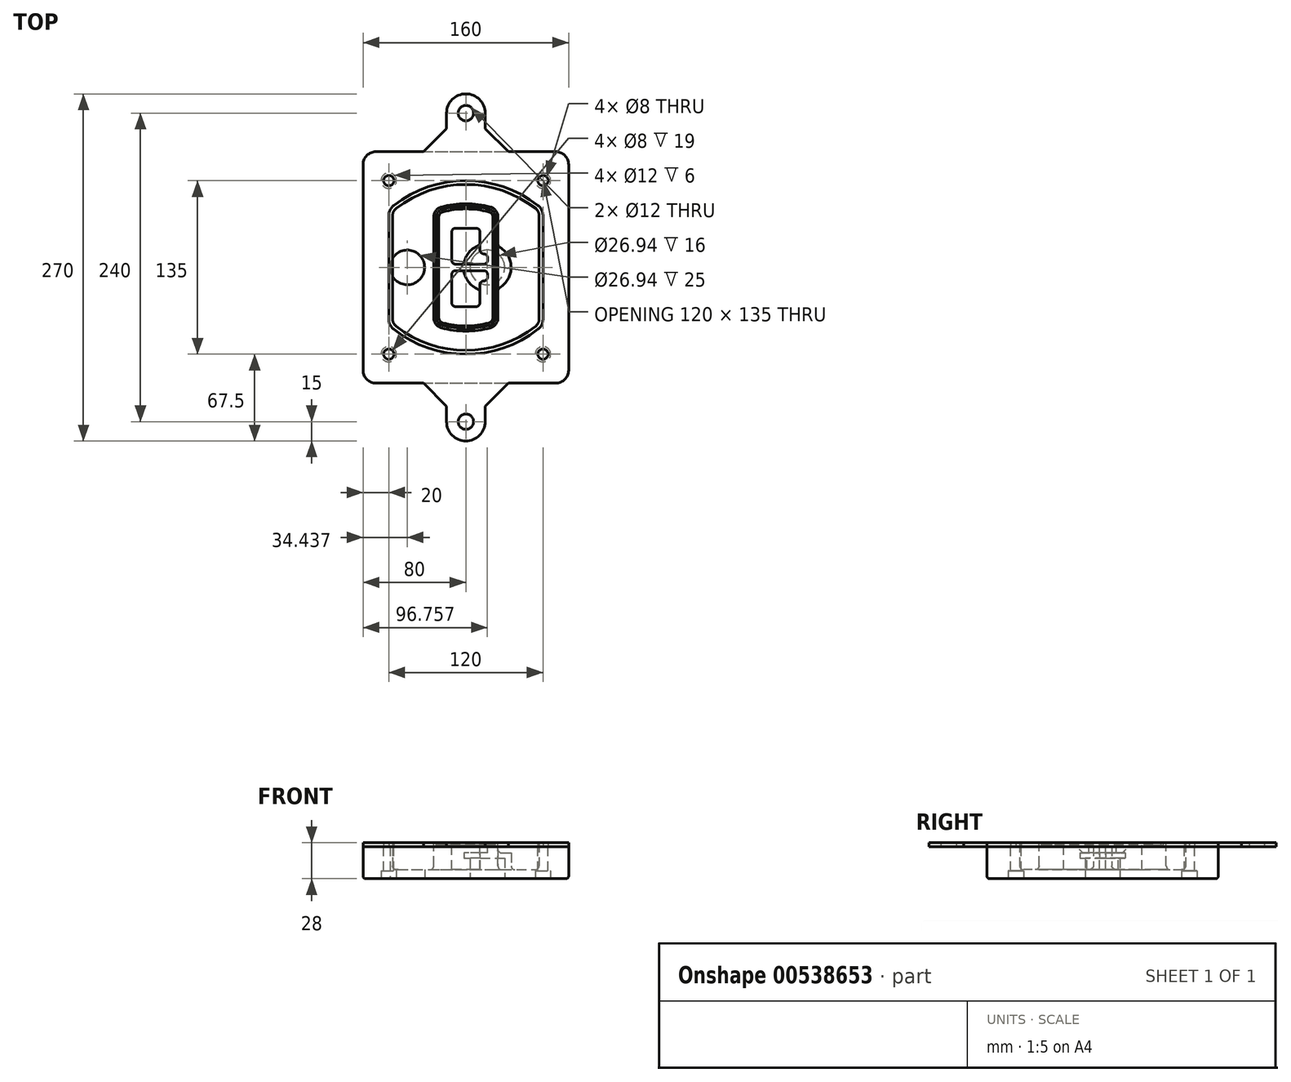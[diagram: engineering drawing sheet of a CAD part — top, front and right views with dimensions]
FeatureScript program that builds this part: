
annotation { "Feature Type Name" : "Feature", "Feature Type Description" : "" }
export const myFeature = defineFeature(function(context is Context, id is Id, definition is map)
    precondition{}
    {
        {
            var Q0;
            Q0=qCreatedBy(makeId("Top.planeOp"),FACE);
            var sketch = newSketch(context, id + "F0", { "sketchPlane" : qUnion([Q0])});
            skPoint(sketch, "E0.rect.middle", {"position": v(0, 0) * mm});
            skLineSegment(sketch, "E1.bottom", {"start": v(-70, -90) * mm, "end": v(70, -90) * mm});
            skLineSegment(sketch, "E1.top", {"start": v(-70, 90) * mm, "end": v(70, 90) * mm});
            skLineSegment(sketch, "E1.left", {"start": v(-80, -80) * mm, "end": v(-80, 80) * mm});
            skLineSegment(sketch, "E1.right", {"start": v(80, -80) * mm, "end": v(80, 80) * mm});
            skLineSegment(sketch, "E2", {"start": v(-80, 90) * mm, "end": v(80, -90) * mm, "construction": true});
            skLineSegment(sketch, "E3", {"start": v(80, 90) * mm, "end": v(-80, -90) * mm, "construction": true});
            skCircle(sketch, "E4", {"center": v(-60, 67.5) * mm, "radius": 4 * mm});
            skCircle(sketch, "E5", {"center": v(60, 67.5) * mm, "radius": 4 * mm});
            skCircle(sketch, "E6", {"center": v(60, -67.5) * mm, "radius": 4 * mm});
            skCircle(sketch, "E7", {"center": v(-60, -67.5) * mm, "radius": 4 * mm});
            skLineSegment(sketch, "E8", {"start": v(-60, 67.5) * mm, "end": v(60, 67.5) * mm, "construction": true});
            skLineSegment(sketch, "E9", {"start": v(60, 67.5) * mm, "end": v(60, -67.5) * mm, "construction": true});
            skLineSegment(sketch, "E10", {"start": v(60, -67.5) * mm, "end": v(-60, -67.5) * mm, "construction": true});
            skLineSegment(sketch, "E11", {"start": v(-60, -67.5) * mm, "end": v(-60, 67.5) * mm, "construction": true});
            skLineSegment(sketch, "E12", {"start": v(-60, 40.3) * mm, "end": v(-60, -40.3) * mm});
            skLineSegment(sketch, "E13", {"start": v(60, 40.3) * mm, "end": v(60, -40.3) * mm});
            skArc(sketch, "E14", {"start": v(56.15, 48.18) * mm, "mid": v(0, 67.5) * mm, "end": v(-56.15, 48.18) * mm});
            skArc(sketch, "E15", {"start": v(-56.15, -48.18) * mm, "mid": v(0, -67.5) * mm, "end": v(56.15, -48.18) * mm});
            skLineSegment(sketch, "E16", {"start": v(-60, 0) * mm, "end": v(60, 0) * mm, "construction": true});
            skPoint(sketch, "E17.visualSharp", {"position": v(-60, -45) * mm});
            skArc(sketch, "E17.filletArc", {"start": v(-60, -40.3) * mm, "mid": v(-58.99, -44.68) * mm, "end": v(-56.15, -48.18) * mm});
            skPoint(sketch, "E18.visualSharp", {"position": v(-60, 45) * mm});
            skArc(sketch, "E18.filletArc", {"start": v(-56.15, 48.18) * mm, "mid": v(-58.99, 44.68) * mm, "end": v(-60, 40.3) * mm});
            skPoint(sketch, "E19.visualSharp", {"position": v(60, 45) * mm});
            skArc(sketch, "E19.filletArc", {"start": v(60, 40.3) * mm, "mid": v(58.99, 44.68) * mm, "end": v(56.15, 48.18) * mm});
            skPoint(sketch, "E20.visualSharp", {"position": v(60, -45) * mm});
            skArc(sketch, "E20.filletArc", {"start": v(56.15, -48.18) * mm, "mid": v(58.99, -44.68) * mm, "end": v(60, -40.3) * mm});
            skPoint(sketch, "E21.visualSharp", {"position": v(-80, 90) * mm});
            skArc(sketch, "E21.filletArc", {"start": v(-70, 90) * mm, "mid": v(-77.07, 87.07) * mm, "end": v(-80, 80) * mm});
            skPoint(sketch, "E22.visualSharp", {"position": v(80, 90) * mm});
            skArc(sketch, "E22.filletArc", {"start": v(80, 80) * mm, "mid": v(77.07, 87.07) * mm, "end": v(70, 90) * mm});
            skPoint(sketch, "E23.visualSharp", {"position": v(80, -90) * mm});
            skArc(sketch, "E23.filletArc", {"start": v(70, -90) * mm, "mid": v(77.07, -87.07) * mm, "end": v(80, -80) * mm});
            skPoint(sketch, "E24.visualSharp", {"position": v(-80, -90) * mm});
            skArc(sketch, "E24.filletArc", {"start": v(-80, -80) * mm, "mid": v(-77.07, -87.07) * mm, "end": v(-70, -90) * mm});
            skArc(sketch, "E25.0", {"start": v(57, 40.3) * mm, "mid": v(56.3, 43.36) * mm, "end": v(54.3, 45.81) * mm});
            skLineSegment(sketch, "E25.1", {"start": v(57, 40.3) * mm, "end": v(57, -40.3) * mm});
            skArc(sketch, "E25.2", {"start": v(54.3, -45.81) * mm, "mid": v(56.3, -43.36) * mm, "end": v(57, -40.3) * mm});
            skArc(sketch, "E25.3", {"start": v(-54.3, -45.81) * mm, "mid": v(0, -64.5) * mm, "end": v(54.3, -45.81) * mm});
            skArc(sketch, "E25.4", {"start": v(-57, -40.3) * mm, "mid": v(-56.3, -43.36) * mm, "end": v(-54.3, -45.81) * mm});
            skArc(sketch, "E25.5", {"start": v(54.3, 45.81) * mm, "mid": v(0, 64.5) * mm, "end": v(-54.3, 45.81) * mm});
            skLineSegment(sketch, "E25.6", {"start": v(-57, 40.3) * mm, "end": v(-57, -40.3) * mm});
            skArc(sketch, "E25.7", {"start": v(-54.3, 45.81) * mm, "mid": v(-56.3, 43.36) * mm, "end": v(-57, 40.3) * mm});
            skArc(sketch, "E26.0", {"start": v(-58.62, 51.33) * mm, "mid": v(-62.58, 46.43) * mm, "end": v(-64, 40.3) * mm});
            skArc(sketch, "E26.1", {"start": v(58.62, 51.33) * mm, "mid": v(0, 71.5) * mm, "end": v(-58.62, 51.33) * mm});
            skArc(sketch, "E26.2", {"start": v(64, 40.3) * mm, "mid": v(62.58, 46.43) * mm, "end": v(58.62, 51.33) * mm});
            skLineSegment(sketch, "E26.3", {"start": v(64, 40.3) * mm, "end": v(64, -40.3) * mm});
            skArc(sketch, "E26.4", {"start": v(58.62, -51.33) * mm, "mid": v(62.58, -46.43) * mm, "end": v(64, -40.3) * mm});
            skLineSegment(sketch, "E26.5", {"start": v(-64, 40.3) * mm, "end": v(-64, -40.3) * mm});
            skArc(sketch, "E26.6", {"start": v(-58.62, -51.33) * mm, "mid": v(0, -71.5) * mm, "end": v(58.62, -51.33) * mm});
            skArc(sketch, "E26.7", {"start": v(-64, -40.3) * mm, "mid": v(-62.58, -46.43) * mm, "end": v(-58.62, -51.33) * mm});
            skSolve(sketch);
        }
        {
            var Q0;
            Q0=makeQuery(id+"F0.imprint","IMPRINT",FACE,{"disambiguationData":[TD([[makeQuery(id+"F0.imprint","IMPRINT",EDGE,{"derivedFrom":sQuery(id+"F0.wireOp",EDGE,"E1.bottom")}),1.0]])]});
            var Q1;
            Q1=makeQuery(id+"F0.imprint","IMPRINT",FACE,{"disambiguationData":[TD([[makeQuery(id+"F0.imprint","IMPRINT",EDGE,{"derivedFrom":sQuery(id+"F0.wireOp",EDGE,"E12")}),1.0]])]});
            var Q2;
            Q2=makeQuery(id+"F0.imprint","IMPRINT",FACE,{"disambiguationData":[TD([[makeQuery(id+"F0.imprint","IMPRINT",EDGE,{"derivedFrom":sQuery(id+"F0.wireOp",EDGE,"E25.0")}),1.0]])]});
            var Q3;
            Q3=makeQuery(id+"F0.imprint","IMPRINT",FACE,{"disambiguationData":[TD([[makeQuery(id+"F0.imprint","IMPRINT",EDGE,{"derivedFrom":sQuery(id+"F0.wireOp",EDGE,"E12")}),-1.0]])]});
            extrude(context, id + "F1", {"entities" : qUnion([Q0, Q1, Q2, Q3]), "oppositeDirection" : true, "depth" : 25 * mm});
        }
        {
            var Q0;
            Q0=makeQuery(id+"F0.imprint","IMPRINT",FACE,{"disambiguationData":[TD([[makeQuery(id+"F0.imprint","IMPRINT",EDGE,{"derivedFrom":sQuery(id+"F0.wireOp",EDGE,"E12")}),1.0]])]});
            extrude(context, id + "F2", {"entities" : qUnion([Q0]), "operationType" : NewBodyOperationType.ADD, "depth" : 3 * mm});
        }
        {
            var Q0;
            Q0=makeQuery(id+"F0.imprint","IMPRINT",FACE,{"disambiguationData":[TD([[makeQuery(id+"F0.imprint","IMPRINT",EDGE,{"derivedFrom":sQuery(id+"F0.wireOp",EDGE,"E25.0")}),1.0]])]});
            extrude(context, id + "F3", {"entities" : qUnion([Q0]), "operationType" : NewBodyOperationType.REMOVE, "oppositeDirection" : true, "depth" : 18 * mm});
        }
        {
            var Q0;
            Q0=makeQuery(id+"F2.opExtrude","CAP_FACE",FACE,{"disambiguationData":[OSD([sQuery(id+"F0.wireOp",EDGE,"E12"),sQuery(id+"F0.wireOp",EDGE,"E13"),sQuery(id+"F0.wireOp",EDGE,"E14"),sQuery(id+"F0.wireOp",EDGE,"E15"),sQuery(id+"F0.wireOp",EDGE,"E17.filletArc"),sQuery(id+"F0.wireOp",EDGE,"E18.filletArc"),sQuery(id+"F0.wireOp",EDGE,"E19.filletArc"),sQuery(id+"F0.wireOp",EDGE,"E20.filletArc"),sQuery(id+"F0.wireOp",EDGE,"E25.0"),sQuery(id+"F0.wireOp",EDGE,"E25.1"),sQuery(id+"F0.wireOp",EDGE,"E25.2"),sQuery(id+"F0.wireOp",EDGE,"E25.3"),sQuery(id+"F0.wireOp",EDGE,"E25.4"),sQuery(id+"F0.wireOp",EDGE,"E25.5"),sQuery(id+"F0.wireOp",EDGE,"E25.6"),sQuery(id+"F0.wireOp",EDGE,"E25.7")])],"isStart":false});
            var sketch = newSketch(context, id + "F4", { "sketchPlane" : qUnion([Q0])});
            skArc(sketch, "E27.0", {"start": v(-19.08, -46.97) * mm, "mid": v(0, -49.5) * mm, "end": v(19.08, -46.97) * mm});
            skArc(sketch, "E28.0", {"start": v(19.08, 46.97) * mm, "mid": v(0, 49.5) * mm, "end": v(-19.08, 46.97) * mm});
            skLineSegment(sketch, "E29", {"start": v(-25, 39.25) * mm, "end": v(-25, -39.25) * mm});
            skLineSegment(sketch, "E30", {"start": v(25, 39.25) * mm, "end": v(25, -39.25) * mm});
            skLineSegment(sketch, "E31", {"start": v(-25, 45.1) * mm, "end": v(25, 45.1) * mm, "construction": true});
            skLineSegment(sketch, "E32", {"start": v(-25, -45.1) * mm, "end": v(25, -45.1) * mm, "construction": true});
            skPoint(sketch, "E33.visualSharp", {"position": v(-25, 45.1) * mm});
            skArc(sketch, "E33.filletArc", {"start": v(-19.08, 46.97) * mm, "mid": v(-23.35, 44.11) * mm, "end": v(-25, 39.25) * mm});
            skPoint(sketch, "E34.visualSharp", {"position": v(25, 45.1) * mm});
            skArc(sketch, "E34.filletArc", {"start": v(25, 39.25) * mm, "mid": v(23.35, 44.11) * mm, "end": v(19.08, 46.97) * mm});
            skPoint(sketch, "E35.visualSharp", {"position": v(25, -45.1) * mm});
            skArc(sketch, "E35.filletArc", {"start": v(19.08, -46.97) * mm, "mid": v(23.35, -44.11) * mm, "end": v(25, -39.25) * mm});
            skPoint(sketch, "E36.visualSharp", {"position": v(-25, -45.1) * mm});
            skArc(sketch, "E36.filletArc", {"start": v(-25, -39.25) * mm, "mid": v(-23.35, -44.11) * mm, "end": v(-19.08, -46.97) * mm});
            skArc(sketch, "E37.0", {"start": v(54.3, 45.81) * mm, "mid": v(0, 64.5) * mm, "end": v(-54.3, 45.81) * mm});
            skArc(sketch, "E37.1", {"start": v(-54.3, 45.81) * mm, "mid": v(-56.3, 43.36) * mm, "end": v(-57, 40.3) * mm});
            skLineSegment(sketch, "E37.2", {"start": v(-57, 40.3) * mm, "end": v(-57, -40.3) * mm});
            skArc(sketch, "E37.3", {"start": v(-57, -40.3) * mm, "mid": v(-56.3, -43.36) * mm, "end": v(-54.3, -45.81) * mm});
            skArc(sketch, "E37.4", {"start": v(-54.3, -45.81) * mm, "mid": v(0, -64.5) * mm, "end": v(54.3, -45.81) * mm});
            skArc(sketch, "E37.5", {"start": v(54.3, -45.81) * mm, "mid": v(56.3, -43.36) * mm, "end": v(57, -40.3) * mm});
            skLineSegment(sketch, "E37.6", {"start": v(57, 40.3) * mm, "end": v(57, -40.3) * mm});
            skArc(sketch, "E37.7", {"start": v(57, 40.3) * mm, "mid": v(56.3, 43.36) * mm, "end": v(54.3, 45.81) * mm});
            skLineSegment(sketch, "E38.0", {"start": v(23, 39.25) * mm, "end": v(23, -39.25) * mm});
            skArc(sketch, "E38.1", {"start": v(18.56, -45.04) * mm, "mid": v(21.76, -42.9) * mm, "end": v(23, -39.25) * mm});
            skArc(sketch, "E38.2", {"start": v(-18.56, -45.04) * mm, "mid": v(0, -47.5) * mm, "end": v(18.56, -45.04) * mm});
            skArc(sketch, "E38.3", {"start": v(-23, -39.25) * mm, "mid": v(-21.76, -42.9) * mm, "end": v(-18.56, -45.04) * mm});
            skLineSegment(sketch, "E38.4", {"start": v(-23, 39.25) * mm, "end": v(-23, -39.25) * mm});
            skArc(sketch, "E38.5", {"start": v(23, 39.25) * mm, "mid": v(21.76, 42.9) * mm, "end": v(18.56, 45.04) * mm});
            skArc(sketch, "E38.6", {"start": v(-18.56, 45.04) * mm, "mid": v(-21.76, 42.9) * mm, "end": v(-23, 39.25) * mm});
            skArc(sketch, "E38.7", {"start": v(18.56, 45.04) * mm, "mid": v(0, 47.5) * mm, "end": v(-18.56, 45.04) * mm});
            skArc(sketch, "E39.0", {"start": v(21, 39.25) * mm, "mid": v(20.18, 41.68) * mm, "end": v(18.04, 43.1) * mm});
            skLineSegment(sketch, "E39.1", {"start": v(21, 39.25) * mm, "end": v(21, -39.25) * mm});
            skArc(sketch, "E39.2", {"start": v(18.04, -43.1) * mm, "mid": v(20.18, -41.68) * mm, "end": v(21, -39.25) * mm});
            skArc(sketch, "E39.3", {"start": v(-18.04, -43.1) * mm, "mid": v(0, -45.5) * mm, "end": v(18.04, -43.1) * mm});
            skArc(sketch, "E39.4", {"start": v(-21, -39.25) * mm, "mid": v(-20.18, -41.68) * mm, "end": v(-18.04, -43.1) * mm});
            skArc(sketch, "E39.5", {"start": v(18.04, 43.1) * mm, "mid": v(0, 45.5) * mm, "end": v(-18.04, 43.1) * mm});
            skLineSegment(sketch, "E39.6", {"start": v(-21, 39.25) * mm, "end": v(-21, -39.25) * mm});
            skArc(sketch, "E39.7", {"start": v(-18.04, 43.1) * mm, "mid": v(-20.18, 41.68) * mm, "end": v(-21, 39.25) * mm});
            skLineSegment(sketch, "E40", {"start": v(-25, 0) * mm, "end": v(25, 0) * mm, "construction": true});
            skLineSegment(sketch, "E41", {"start": v(-11, 5.5) * mm, "end": v(-11, 27.5) * mm});
            skLineSegment(sketch, "E42", {"start": v(-8, 30.5) * mm, "end": v(8, 30.5) * mm});
            skLineSegment(sketch, "E43", {"start": v(11, 27.5) * mm, "end": v(11, 13.5) * mm});
            skLineSegment(sketch, "E44", {"start": v(14, 10.5) * mm, "end": v(14, 10.5) * mm});
            skLineSegment(sketch, "E45", {"start": v(17, 7.5) * mm, "end": v(17, 5.5) * mm});
            skLineSegment(sketch, "E46", {"start": v(14, 2.5) * mm, "end": v(-8, 2.5) * mm});
            skPoint(sketch, "E47.visualSharp", {"position": v(-11, 30.5) * mm});
            skArc(sketch, "E47.filletArc", {"start": v(-8, 30.5) * mm, "mid": v(-10.12, 29.62) * mm, "end": v(-11, 27.5) * mm});
            skPoint(sketch, "E48.visualSharp", {"position": v(11, 30.5) * mm});
            skArc(sketch, "E48.filletArc", {"start": v(11, 27.5) * mm, "mid": v(10.12, 29.62) * mm, "end": v(8, 30.5) * mm});
            skPoint(sketch, "E49.visualSharp", {"position": v(11, 10.5) * mm});
            skArc(sketch, "E49.filletArc", {"start": v(11, 13.5) * mm, "mid": v(11.88, 11.38) * mm, "end": v(14, 10.5) * mm});
            skPoint(sketch, "E50.visualSharp", {"position": v(17, 10.5) * mm});
            skArc(sketch, "E50.filletArc", {"start": v(17, 7.5) * mm, "mid": v(16.12, 9.62) * mm, "end": v(14, 10.5) * mm});
            skPoint(sketch, "E51.visualSharp", {"position": v(17, 2.5) * mm});
            skArc(sketch, "E51.filletArc", {"start": v(14, 2.5) * mm, "mid": v(16.12, 3.38) * mm, "end": v(17, 5.5) * mm});
            skPoint(sketch, "E52.visualSharp", {"position": v(-11, 2.5) * mm});
            skArc(sketch, "E52.filletArc", {"start": v(-11, 5.5) * mm, "mid": v(-10.12, 3.38) * mm, "end": v(-8, 2.5) * mm});
            skLineSegment(sketch, "E53.0.MirrorCS", {"start": v(14, -2.5) * mm, "end": v(-8, -2.5) * mm});
            skArc(sketch, "E54.0.MirrorCS", {"start": v(-11, -5.5) * mm, "mid": v(-10.12, -3.38) * mm, "end": v(-8, -2.5) * mm});
            skLineSegment(sketch, "E55.0.MirrorCS", {"start": v(-11, -5.5) * mm, "end": v(-11, -27.5) * mm});
            skArc(sketch, "E56.0.MirrorCS", {"start": v(-8, -30.5) * mm, "mid": v(-10.12, -29.62) * mm, "end": v(-11, -27.5) * mm});
            skLineSegment(sketch, "E57.0.MirrorCS", {"start": v(-8, -30.5) * mm, "end": v(8, -30.5) * mm});
            skArc(sketch, "E58.0.MirrorCS", {"start": v(11, -27.5) * mm, "mid": v(10.12, -29.62) * mm, "end": v(8, -30.5) * mm});
            skLineSegment(sketch, "E59.0.MirrorCS", {"start": v(11, -27.5) * mm, "end": v(11, -13.5) * mm});
            skArc(sketch, "E60.0.MirrorCS", {"start": v(11, -13.5) * mm, "mid": v(11.88, -11.38) * mm, "end": v(14, -10.5) * mm});
            skArc(sketch, "E61.0.MirrorCS", {"start": v(17, -7.5) * mm, "mid": v(16.12, -9.62) * mm, "end": v(14, -10.5) * mm});
            skLineSegment(sketch, "E62.0.MirrorCS", {"start": v(17, -7.5) * mm, "end": v(17, -5.5) * mm});
            skArc(sketch, "E63.0.MirrorCS", {"start": v(14, -2.5) * mm, "mid": v(16.12, -3.38) * mm, "end": v(17, -5.5) * mm});
            skSolve(sketch);
        }
        {
            var Q0;
            Q0=makeQuery(id+"F4.imprint","IMPRINT",FACE,{"disambiguationData":[TD([[makeQuery(id+"F4.imprint","IMPRINT",EDGE,{"derivedFrom":sQuery(id+"F4.wireOp",EDGE,"E27.0")}),1.0]])]});
            var Q1;
            Q1=makeQuery(id+"F4.imprint","IMPRINT",FACE,{"disambiguationData":[TD([[makeQuery(id+"F4.imprint","IMPRINT",EDGE,{"derivedFrom":sQuery(id+"F4.wireOp",EDGE,"E38.0")}),-1.0]])]});
            var Q2;
            Q2=makeQuery(id+"F4.imprint","IMPRINT",FACE,{"disambiguationData":[TD([[makeQuery(id+"F4.imprint","IMPRINT",EDGE,{"derivedFrom":sQuery(id+"F4.wireOp",EDGE,"E39.0")}),1.0]])]});
            extrude(context, id + "F5", {"entities" : qUnion([Q0, Q1, Q2]), "operationType" : NewBodyOperationType.ADD, "endBound" : BoundingType.UP_TO_NEXT, "oppositeDirection" : true, "depth" : 25 * mm});
        }
        {
            var Q0;
            Q0=makeQuery(id+"F4.imprint","IMPRINT",FACE,{"disambiguationData":[TD([[makeQuery(id+"F4.imprint","IMPRINT",EDGE,{"derivedFrom":sQuery(id+"F4.wireOp",EDGE,"E38.0")}),-1.0]])]});
            extrude(context, id + "F6", {"entities" : qUnion([Q0]), "operationType" : NewBodyOperationType.REMOVE, "oppositeDirection" : true, "depth" : 2 * mm});
        }
        {
            var Q0;
            Q0=makeQuery(id+"F1.opExtrude","CAP_FACE",FACE,{"disambiguationData":[OSD([sQuery(id+"F0.wireOp",EDGE,"E1.bottom"),sQuery(id+"F0.wireOp",EDGE,"E1.top"),sQuery(id+"F0.wireOp",EDGE,"E1.left"),sQuery(id+"F0.wireOp",EDGE,"E1.right"),sQuery(id+"F0.wireOp",EDGE,"E4"),sQuery(id+"F0.wireOp",EDGE,"E5"),sQuery(id+"F0.wireOp",EDGE,"E6"),sQuery(id+"F0.wireOp",EDGE,"E7"),sQuery(id+"F0.wireOp",EDGE,"E21.filletArc"),sQuery(id+"F0.wireOp",EDGE,"E22.filletArc"),sQuery(id+"F0.wireOp",EDGE,"E23.filletArc"),sQuery(id+"F0.wireOp",EDGE,"E24.filletArc")])],"isStart":false});
            var sketch = newSketch(context, id + "F7", { "sketchPlane" : qUnion([Q0])});
            skCircle(sketch, "E64", {"center": v(16.76, 0) * mm, "radius": 13.47 * mm});
            skCircle(sketch, "E65", {"center": v(-45.56, 0) * mm, "radius": 13.47 * mm});
            skLineSegment(sketch, "E66", {"start": v(80, 0) * mm, "end": v(-80, 0) * mm});
            skCircle(sketch, "E67", {"center": v(16.76, 0) * mm, "radius": 18.47 * mm});
            skCircle(sketch, "E68", {"center": v(60, -67.5) * mm, "radius": 6 * mm});
            skCircle(sketch, "E69", {"center": v(-60, -67.5) * mm, "radius": 6 * mm});
            skCircle(sketch, "E70", {"center": v(-60, 67.5) * mm, "radius": 6 * mm});
            skCircle(sketch, "E71", {"center": v(60, 67.5) * mm, "radius": 6 * mm});
            skSolve(sketch);
        }
        {
            var Q0;
            {var subQ1=sQuery(id+"F7.wireOp",EDGE,"E66");var subQ4=sQuery(id+"F7.wireOp",EDGE,"E64");var subQ6=makeQuery(id+"F7.imprint","INTERSECT",VERTEX,{"disambiguationData":[OD(0.0)],"derivedFrom":[subQ4,subQ1]});Q0=makeQuery(id+"F7.imprint","IMPRINT",FACE,{"disambiguationData":[TD([[makeQuery(id+"F7.imprint","IMPRINT",EDGE,{"disambiguationData":[TD([[subQ6,-1.0]])],"derivedFrom":subQ4}),-1.0]])]});}
            var Q1;
            {var subQ0=sQuery(id+"F7.wireOp",EDGE,"E66");var subQ1=sQuery(id+"F7.wireOp",EDGE,"E64");var subQ3=makeQuery(id+"F7.imprint","INTERSECT",VERTEX,{"disambiguationData":[OD(0.0)],"derivedFrom":[subQ1,subQ0]});Q1=makeQuery(id+"F7.imprint","IMPRINT",FACE,{"disambiguationData":[TD([[makeQuery(id+"F7.imprint","IMPRINT",EDGE,{"disambiguationData":[TD([[subQ3,-1.0]])],"derivedFrom":subQ1}),1.0]])]});}
            var Q2;
            {var subQ0=sQuery(id+"F7.wireOp",EDGE,"E66");var subQ1=sQuery(id+"F7.wireOp",EDGE,"E64");var subQ3=makeQuery(id+"F7.imprint","INTERSECT",VERTEX,{"disambiguationData":[OD(0.0)],"derivedFrom":[subQ1,subQ0]});Q2=makeQuery(id+"F7.imprint","IMPRINT",FACE,{"disambiguationData":[TD([[makeQuery(id+"F7.imprint","IMPRINT",EDGE,{"disambiguationData":[TD([[subQ3,1.0]])],"derivedFrom":subQ1}),1.0]])]});}
            var Q3;
            {var subQ1=sQuery(id+"F7.wireOp",EDGE,"E66");var subQ4=sQuery(id+"F7.wireOp",EDGE,"E64");var subQ6=makeQuery(id+"F7.imprint","INTERSECT",VERTEX,{"disambiguationData":[OD(0.0)],"derivedFrom":[subQ4,subQ1]});Q3=makeQuery(id+"F7.imprint","IMPRINT",FACE,{"disambiguationData":[TD([[makeQuery(id+"F7.imprint","IMPRINT",EDGE,{"disambiguationData":[TD([[subQ6,1.0]])],"derivedFrom":subQ4}),-1.0]])]});}
            extrude(context, id + "F8", {"entities" : qUnion([Q0, Q1, Q2, Q3]), "operationType" : NewBodyOperationType.ADD, "oppositeDirection" : true, "depth" : 20 * mm});
        }
        {
            var Q0;
            {var subQ0=sQuery(id+"F7.wireOp",EDGE,"E66");var subQ1=sQuery(id+"F7.wireOp",EDGE,"E64");var subQ3=makeQuery(id+"F7.imprint","INTERSECT",VERTEX,{"disambiguationData":[OD(0.0)],"derivedFrom":[subQ1,subQ0]});Q0=makeQuery(id+"F7.imprint","IMPRINT",FACE,{"disambiguationData":[TD([[makeQuery(id+"F7.imprint","IMPRINT",EDGE,{"disambiguationData":[TD([[subQ3,-1.0]])],"derivedFrom":subQ1}),1.0]])]});}
            var Q1;
            {var subQ0=sQuery(id+"F7.wireOp",EDGE,"E66");var subQ1=sQuery(id+"F7.wireOp",EDGE,"E64");var subQ3=makeQuery(id+"F7.imprint","INTERSECT",VERTEX,{"disambiguationData":[OD(0.0)],"derivedFrom":[subQ1,subQ0]});Q1=makeQuery(id+"F7.imprint","IMPRINT",FACE,{"disambiguationData":[TD([[makeQuery(id+"F7.imprint","IMPRINT",EDGE,{"disambiguationData":[TD([[subQ3,1.0]])],"derivedFrom":subQ1}),1.0]])]});}
            extrude(context, id + "F9", {"entities" : qUnion([Q0, Q1]), "operationType" : NewBodyOperationType.REMOVE, "oppositeDirection" : true, "depth" : 16 * mm});
        }
        {
            var Q0;
            {var subQ0=sQuery(id+"F7.wireOp",EDGE,"E66");var subQ1=sQuery(id+"F7.wireOp",EDGE,"E65");var subQ3=makeQuery(id+"F7.imprint","INTERSECT",VERTEX,{"disambiguationData":[OD(0.0)],"derivedFrom":[subQ1,subQ0]});Q0=makeQuery(id+"F7.imprint","IMPRINT",FACE,{"disambiguationData":[TD([[makeQuery(id+"F7.imprint","IMPRINT",EDGE,{"disambiguationData":[TD([[subQ3,-1.0]])],"derivedFrom":subQ1}),1.0]])]});}
            var Q1;
            {var subQ0=sQuery(id+"F7.wireOp",EDGE,"E66");var subQ1=sQuery(id+"F7.wireOp",EDGE,"E65");var subQ3=makeQuery(id+"F7.imprint","INTERSECT",VERTEX,{"disambiguationData":[OD(0.0)],"derivedFrom":[subQ1,subQ0]});Q1=makeQuery(id+"F7.imprint","IMPRINT",FACE,{"disambiguationData":[TD([[makeQuery(id+"F7.imprint","IMPRINT",EDGE,{"disambiguationData":[TD([[subQ3,1.0]])],"derivedFrom":subQ1}),1.0]])]});}
            extrude(context, id + "F10", {"entities" : qUnion([Q0, Q1]), "operationType" : NewBodyOperationType.REMOVE, "oppositeDirection" : true, "depth" : 25 * mm});
        }
        {
            var Q0;
            Q0=makeQuery(id+"F7.imprint","IMPRINT",FACE,{"disambiguationData":[TD([[makeQuery(id+"F7.imprint","IMPRINT",EDGE,{"derivedFrom":sQuery(id+"F7.wireOp",EDGE,"E68")}),1.0]])]});
            var Q1;
            Q1=makeQuery(id+"F7.imprint","IMPRINT",FACE,{"disambiguationData":[TD([[makeQuery(id+"F7.imprint","IMPRINT",EDGE,{"derivedFrom":makeQuery(id+"F1.opExtrude","CAP_EDGE",EDGE,{"disambiguationData":[OSD([sQuery(id+"F0.wireOp",EDGE,"E5")])],"isStart":false})}),-1.0]])]});
            var Q2;
            Q2=makeQuery(id+"F7.imprint","IMPRINT",FACE,{"disambiguationData":[TD([[makeQuery(id+"F7.imprint","IMPRINT",EDGE,{"derivedFrom":sQuery(id+"F7.wireOp",EDGE,"E69")}),1.0]])]});
            var Q3;
            Q3=makeQuery(id+"F7.imprint","IMPRINT",FACE,{"disambiguationData":[TD([[makeQuery(id+"F7.imprint","IMPRINT",EDGE,{"derivedFrom":makeQuery(id+"F1.opExtrude","CAP_EDGE",EDGE,{"disambiguationData":[OSD([sQuery(id+"F0.wireOp",EDGE,"E4")])],"isStart":false})}),-1.0]])]});
            var Q4;
            Q4=makeQuery(id+"F7.imprint","IMPRINT",FACE,{"disambiguationData":[TD([[makeQuery(id+"F7.imprint","IMPRINT",EDGE,{"derivedFrom":sQuery(id+"F7.wireOp",EDGE,"E70")}),1.0]])]});
            var Q5;
            Q5=makeQuery(id+"F7.imprint","IMPRINT",FACE,{"disambiguationData":[TD([[makeQuery(id+"F7.imprint","IMPRINT",EDGE,{"derivedFrom":makeQuery(id+"F1.opExtrude","CAP_EDGE",EDGE,{"disambiguationData":[OSD([sQuery(id+"F0.wireOp",EDGE,"E7")])],"isStart":false})}),-1.0]])]});
            var Q6;
            Q6=makeQuery(id+"F7.imprint","IMPRINT",FACE,{"disambiguationData":[TD([[makeQuery(id+"F7.imprint","IMPRINT",EDGE,{"derivedFrom":sQuery(id+"F7.wireOp",EDGE,"E71")}),1.0]])]});
            var Q7;
            Q7=makeQuery(id+"F7.imprint","IMPRINT",FACE,{"disambiguationData":[TD([[makeQuery(id+"F7.imprint","IMPRINT",EDGE,{"derivedFrom":makeQuery(id+"F1.opExtrude","CAP_EDGE",EDGE,{"disambiguationData":[OSD([sQuery(id+"F0.wireOp",EDGE,"E6")])],"isStart":false})}),-1.0]])]});
            extrude(context, id + "F11", {"entities" : qUnion([Q0, Q1, Q2, Q3, Q4, Q5, Q6, Q7]), "operationType" : NewBodyOperationType.REMOVE, "oppositeDirection" : true, "depth" : 6 * mm});
        }
        {
            var Q0;
            Q0=makeQuery(id+"F9.boolean.opBoolean","COPY",FACE,{"derivedFrom":makeQuery(id+"F9.opExtrude","CAP_FACE",FACE,{"disambiguationData":[OSD([sQuery(id+"F7.wireOp",EDGE,"E64")])],"isStart":false})});
            var sketch = newSketch(context, id + "F12", { "sketchPlane" : qUnion([Q0])});
            skArc(sketch, "E72.0", {"start": v(11, 17.55) * mm, "mid": v(2.57, 11.82) * mm, "end": v(-1.54, 2.5) * mm});
            skArc(sketch, "E72.1", {"start": v(-1.54, -2.5) * mm, "mid": v(2.57, -11.82) * mm, "end": v(11, -17.55) * mm});
            skLineSegment(sketch, "E73", {"start": v(-1.54, -2.5) * mm, "end": v(14, -2.5) * mm});
            skLineSegment(sketch, "E74.0", {"start": v(14, 2.5) * mm, "end": v(-1.54, 2.5) * mm});
            skArc(sketch, "E74.1", {"start": v(14, 2.5) * mm, "mid": v(16.12, 3.38) * mm, "end": v(17, 5.5) * mm});
            skLineSegment(sketch, "E74.2", {"start": v(17, 7.5) * mm, "end": v(17, 5.5) * mm});
            skArc(sketch, "E74.3", {"start": v(17, 7.5) * mm, "mid": v(16.12, 9.62) * mm, "end": v(14, 10.5) * mm});
            skArc(sketch, "E74.4", {"start": v(11, 13.5) * mm, "mid": v(11.88, 11.38) * mm, "end": v(14, 10.5) * mm});
            skLineSegment(sketch, "E74.5", {"start": v(11, 17.55) * mm, "end": v(11, 13.5) * mm});
            skLineSegment(sketch, "E74.7", {"start": v(14, -2.5) * mm, "end": v(-1.54, -2.5) * mm});
            skArc(sketch, "E74.8", {"start": v(14, -2.5) * mm, "mid": v(16.12, -3.38) * mm, "end": v(17, -5.5) * mm});
            skLineSegment(sketch, "E74.9", {"start": v(17, -7.5) * mm, "end": v(17, -5.5) * mm});
            skArc(sketch, "E74.10", {"start": v(17, -7.5) * mm, "mid": v(16.12, -9.62) * mm, "end": v(14, -10.5) * mm});
            skArc(sketch, "E74.11", {"start": v(11, -13.5) * mm, "mid": v(11.88, -11.38) * mm, "end": v(14, -10.5) * mm});
            skLineSegment(sketch, "E74.12", {"start": v(11, -17.55) * mm, "end": v(11, -13.5) * mm});
            skPoint(sketch, "E75.orphan", {"position": v(11, -27.5) * mm});
            skPoint(sketch, "E76.orphan", {"position": v(-8, -2.5) * mm});
            skPoint(sketch, "E77.orphan", {"position": v(-8, 2.5) * mm});
            skPoint(sketch, "E78.orphan", {"position": v(11, 27.5) * mm});
            skSolve(sketch);
        }
        {
            var Q0;
            {var subQ7=sQuery(id+"F12.wireOp",EDGE,"E72.0");var subQ14=sQuery(id+"F12.wireOp",EDGE,"E72.1");var subQ16=sQuery(id+"F12.wireOp",EDGE,"E74.1");var subQ18=sQuery(id+"F12.wireOp",EDGE,"E74.8");Q0=qUnion([makeQuery(id+"F12.imprint","IMPRINT",FACE,{"disambiguationData":[TD([[makeQuery(id+"F12.imprint","IMPRINT",EDGE,{"derivedFrom":subQ7}),1.0]])]}),makeQuery(id+"F12.imprint","IMPRINT",FACE,{"disambiguationData":[TD([[makeQuery(id+"F12.imprint","IMPRINT",EDGE,{"derivedFrom":subQ14}),1.0]])]}),makeQuery(id+"F12.imprint","IMPRINT",FACE,{"disambiguationData":[TD([[makeQuery(id+"F12.imprint","IMPRINT",EDGE,{"derivedFrom":subQ16}),1.0]])]}),makeQuery(id+"F12.imprint","IMPRINT",FACE,{"disambiguationData":[TD([[makeQuery(id+"F12.imprint","IMPRINT",EDGE,{"derivedFrom":subQ18}),-1.0]])]})]);}
            var Q1;
            Q1=makeQuery(id+"F5.boolean.opBoolean","SPLIT",FACE,{"disambiguationData":[TD([makeQuery(id+"F5.opExtrude","SWEPT_FACE",FACE,{"disambiguationData":[OSD([sQuery(id+"F4.wireOp",EDGE,"E41")])]})])],"derivedFrom":makeQuery(id+"F3.boolean.opBoolean","COPY",FACE,{"derivedFrom":makeQuery(id+"F3.opExtrude","CAP_FACE",FACE,{"disambiguationData":[OSD([sQuery(id+"F0.wireOp",EDGE,"E25.0"),sQuery(id+"F0.wireOp",EDGE,"E25.1"),sQuery(id+"F0.wireOp",EDGE,"E25.2"),sQuery(id+"F0.wireOp",EDGE,"E25.3"),sQuery(id+"F0.wireOp",EDGE,"E25.4"),sQuery(id+"F0.wireOp",EDGE,"E25.5"),sQuery(id+"F0.wireOp",EDGE,"E25.6"),sQuery(id+"F0.wireOp",EDGE,"E25.7")])],"isStart":false})})});
            extrude(context, id + "F13", {"entities" : qUnion([Q0]), "operationType" : NewBodyOperationType.REMOVE, "endBound" : BoundingType.UP_TO_SURFACE, "endBoundEntityFace" : qUnion([Q1]), "depth" : 25 * mm});
        }
        {
            var Q0;
            Q0=makeQuery(id+"F3.boolean.opBoolean","COPY",EDGE,{"derivedFrom":makeQuery(id+"F3.opExtrude","CAP_EDGE",EDGE,{"disambiguationData":[OSD([sQuery(id+"F0.wireOp",EDGE,"E25.6")])],"isStart":false})});
            var Q1;
            Q1=makeQuery(id+"F8.boolean.opBoolean","INTERSECT",EDGE,{"derivedFrom":[makeQuery(id+"F5.opExtrude","SWEPT_FACE",FACE,{"disambiguationData":[OSD([sQuery(id+"F4.wireOp",EDGE,"E30")])]}),makeQuery(id+"F8.opExtrude","CAP_FACE",FACE,{"disambiguationData":[OSD([sQuery(id+"F7.wireOp",EDGE,"E67")])],"isStart":false})]});
            var Q2;
            Q2=makeQuery(id+"F8.boolean.opBoolean","INTERSECT",EDGE,{"disambiguationData":[OD(1.0)],"derivedFrom":[makeQuery(id+"F5.opExtrude","SWEPT_FACE",FACE,{"disambiguationData":[OSD([sQuery(id+"F4.wireOp",EDGE,"E30")])]}),makeQuery(id+"F8.opExtrude","SWEPT_FACE",FACE,{"disambiguationData":[OSD([sQuery(id+"F7.wireOp",EDGE,"E67")])]})]});
            var Q3;
            {var subQ0=sQuery(id+"F4.wireOp",EDGE,"E30");Q3=makeQuery(id+"F8.boolean.opBoolean","SPLIT",EDGE,{"disambiguationData":[TD([makeQuery(id+"F5.opExtrude","SWEPT_FACE",FACE,{"disambiguationData":[OSD([sQuery(id+"F4.wireOp",EDGE,"E35.filletArc")])]})])],"derivedFrom":makeQuery(id+"F5.opExtrude","CAP_EDGE",EDGE,{"disambiguationData":[OSD([subQ0])],"isStart":false})});}
            var Q4;
            {var subQ0=sQuery(id+"F0.wireOp",EDGE,"E25.7");var subQ1=sQuery(id+"F0.wireOp",EDGE,"E25.1");var subQ2=sQuery(id+"F0.wireOp",EDGE,"E25.6");var subQ3=sQuery(id+"F0.wireOp",EDGE,"E25.5");var subQ4=sQuery(id+"F0.wireOp",EDGE,"E25.4");var subQ5=sQuery(id+"F0.wireOp",EDGE,"E25.0");var subQ6=sQuery(id+"F0.wireOp",EDGE,"E25.2");var subQ7=sQuery(id+"F0.wireOp",EDGE,"E25.3");Q4=makeQuery(id+"F8.boolean.opBoolean","INTERSECT",EDGE,{"derivedFrom":[makeQuery(id+"F5.boolean.opBoolean","SPLIT",FACE,{"disambiguationData":[TD([makeQuery(id+"F2.opExtrude","SWEPT_FACE",FACE,{"disambiguationData":[OSD([subQ5])]})])],"derivedFrom":makeQuery(id+"F3.boolean.opBoolean","COPY",FACE,{"derivedFrom":makeQuery(id+"F3.opExtrude","CAP_FACE",FACE,{"disambiguationData":[OSD([subQ5,subQ1,subQ6,subQ7,subQ4,subQ3,subQ2,subQ0])],"isStart":false})})}),makeQuery(id+"F8.opExtrude","SWEPT_FACE",FACE,{"disambiguationData":[OSD([sQuery(id+"F7.wireOp",EDGE,"E67")])]})]});}
            var Q5;
            Q5=makeQuery(id+"F8.boolean.opBoolean","INTERSECT",EDGE,{"disambiguationData":[OD(0.0)],"derivedFrom":[makeQuery(id+"F5.opExtrude","SWEPT_FACE",FACE,{"disambiguationData":[OSD([sQuery(id+"F4.wireOp",EDGE,"E30")])]}),makeQuery(id+"F8.opExtrude","SWEPT_FACE",FACE,{"disambiguationData":[OSD([sQuery(id+"F7.wireOp",EDGE,"E67")])]})]});
            fillet(context, id + "F14", {"entities" : qUnion([Q0, Q1, Q2, Q3, Q4, Q5]), "radius" : 3 * mm, "tangentPropagation" : true, "allowEdgeOverflow" : false});
        }
        {
            var Q0;
            Q0=makeQuery(id+"F1.opExtrude","CAP_EDGE",EDGE,{"disambiguationData":[OSD([sQuery(id+"F0.wireOp",EDGE,"E1.bottom")])],"isStart":false});
            fillet(context, id + "F15", {"entities" : qUnion([Q0]), "radius" : 2 * mm, "tangentPropagation" : true, "allowEdgeOverflow" : false});
        }
        {
            var Q0;
            {var subQ0=sQuery(id+"F0.wireOp",EDGE,"E21.filletArc");var subQ1=sQuery(id+"F0.wireOp",EDGE,"E7");var subQ2=sQuery(id+"F0.wireOp",EDGE,"E6");var subQ3=sQuery(id+"F0.wireOp",EDGE,"E5");var subQ4=sQuery(id+"F0.wireOp",EDGE,"E4");var subQ5=sQuery(id+"F0.wireOp",EDGE,"E22.filletArc");var subQ6=sQuery(id+"F0.wireOp",EDGE,"E1.bottom");var subQ7=sQuery(id+"F0.wireOp",EDGE,"E1.right");var subQ8=sQuery(id+"F0.wireOp",EDGE,"E1.top");var subQ9=sQuery(id+"F0.wireOp",EDGE,"E1.left");var subQ10=sQuery(id+"F0.wireOp",EDGE,"E23.filletArc");var subQ11=sQuery(id+"F0.wireOp",EDGE,"E24.filletArc");Q0=makeQuery(id+"F2.boolean.opBoolean","SPLIT",FACE,{"disambiguationData":[TD([makeQuery(id+"F1.opExtrude","SWEPT_FACE",FACE,{"disambiguationData":[OSD([subQ6])]})])],"derivedFrom":makeQuery(id+"F1.opExtrude","CAP_FACE",FACE,{"disambiguationData":[OSD([subQ6,subQ8,subQ9,subQ7,subQ4,subQ3,subQ2,subQ1,subQ0,subQ5,subQ10,subQ11])],"isStart":true})});}
            var sketch = newSketch(context, id + "F16", { "sketchPlane" : qUnion([Q0])});
            skLineSegment(sketch, "E79.0", {"start": v(-70, 90) * mm, "end": v(70, 90) * mm});
            skArc(sketch, "E80.0", {"start": v(-70, 90) * mm, "mid": v(-77.07, 87.07) * mm, "end": v(-80, 80) * mm});
            skArc(sketch, "E80.1", {"start": v(80, 80) * mm, "mid": v(77.07, 87.07) * mm, "end": v(70, 90) * mm});
            skLineSegment(sketch, "E80.2", {"start": v(80, -80) * mm, "end": v(80, 80) * mm});
            skLineSegment(sketch, "E80.3", {"start": v(-80, -80) * mm, "end": v(-80, 80) * mm});
            skCircle(sketch, "E80.4", {"center": v(-60, 67.5) * mm, "radius": 4 * mm});
            skCircle(sketch, "E80.5", {"center": v(60, 67.5) * mm, "radius": 4 * mm});
            skArc(sketch, "E80.6", {"start": v(56.15, 48.18) * mm, "mid": v(0, 67.5) * mm, "end": v(-56.15, 48.18) * mm});
            skArc(sketch, "E80.7", {"start": v(60, 40.3) * mm, "mid": v(58.99, 44.68) * mm, "end": v(56.15, 48.18) * mm});
            skLineSegment(sketch, "E80.8", {"start": v(60, 40.3) * mm, "end": v(60, -40.3) * mm});
            skArc(sketch, "E80.9", {"start": v(56.15, -48.18) * mm, "mid": v(58.99, -44.68) * mm, "end": v(60, -40.3) * mm});
            skArc(sketch, "E80.10", {"start": v(-56.15, -48.18) * mm, "mid": v(0, -67.5) * mm, "end": v(56.15, -48.18) * mm});
            skArc(sketch, "E80.11", {"start": v(-60, -40.3) * mm, "mid": v(-58.99, -44.68) * mm, "end": v(-56.15, -48.18) * mm});
            skLineSegment(sketch, "E80.12", {"start": v(-60, 40.3) * mm, "end": v(-60, -40.3) * mm});
            skArc(sketch, "E80.13", {"start": v(-56.15, 48.18) * mm, "mid": v(-58.99, 44.68) * mm, "end": v(-60, 40.3) * mm});
            skCircle(sketch, "E80.14", {"center": v(60, -67.5) * mm, "radius": 4 * mm});
            skCircle(sketch, "E80.15", {"center": v(-60, -67.5) * mm, "radius": 4 * mm});
            skArc(sketch, "E80.16", {"start": v(-80, -80) * mm, "mid": v(-77.07, -87.07) * mm, "end": v(-70, -90) * mm});
            skLineSegment(sketch, "E80.17", {"start": v(-70, -90) * mm, "end": v(70, -90) * mm});
            skArc(sketch, "E80.18", {"start": v(70, -90) * mm, "mid": v(77.07, -87.07) * mm, "end": v(80, -80) * mm});
            skLineSegment(sketch, "E81", {"start": v(0, 90) * mm, "end": v(0, 120) * mm, "construction": true});
            skCircle(sketch, "E82", {"center": v(0, 120) * mm, "radius": 6 * mm});
            skArc(sketch, "E83", {"start": v(15, 120) * mm, "mid": v(0, 135) * mm, "end": v(-15, 120) * mm});
            skLineSegment(sketch, "E84", {"start": v(15, 120) * mm, "end": v(15, 108) * mm});
            skLineSegment(sketch, "E85", {"start": v(15, 108) * mm, "end": v(33, 90) * mm});
            skLineSegment(sketch, "E86", {"start": v(-15, 120) * mm, "end": v(-15, 108) * mm});
            skLineSegment(sketch, "E87", {"start": v(-15, 108) * mm, "end": v(-33, 90) * mm});
            skLineSegment(sketch, "E88", {"start": v(-80, 0) * mm, "end": v(80, 0) * mm, "construction": true});
            skLineSegment(sketch, "E89.MirrorCS", {"start": v(15, -108) * mm, "end": v(33, -90) * mm});
            skLineSegment(sketch, "E90.MirrorCS", {"start": v(15, -120) * mm, "end": v(15, -108) * mm});
            skCircle(sketch, "E91.MirrorC", {"center": v(0, -120) * mm, "radius": 6 * mm});
            skLineSegment(sketch, "E92.MirrorCS", {"start": v(0, -90) * mm, "end": v(0, -120) * mm, "construction": true});
            skArc(sketch, "E93.MirrorCS", {"start": v(15, -120) * mm, "mid": v(0, -135) * mm, "end": v(-15, -120) * mm});
            skLineSegment(sketch, "E94.MirrorCS", {"start": v(-15, -120) * mm, "end": v(-15, -108) * mm});
            skLineSegment(sketch, "E95.MirrorCS", {"start": v(-15, -108) * mm, "end": v(-33, -90) * mm});
            skSolve(sketch);
        }
        {
            var Q0;
            Q0 = qSketchRegion(id + "F16", true);
            var Q1;
            Q1=makeQuery(id+"F2.opExtrude","CAP_FACE",FACE,{"disambiguationData":[OSD([sQuery(id+"F0.wireOp",EDGE,"E12"),sQuery(id+"F0.wireOp",EDGE,"E13"),sQuery(id+"F0.wireOp",EDGE,"E14"),sQuery(id+"F0.wireOp",EDGE,"E15"),sQuery(id+"F0.wireOp",EDGE,"E17.filletArc"),sQuery(id+"F0.wireOp",EDGE,"E18.filletArc"),sQuery(id+"F0.wireOp",EDGE,"E19.filletArc"),sQuery(id+"F0.wireOp",EDGE,"E20.filletArc"),sQuery(id+"F0.wireOp",EDGE,"E25.0"),sQuery(id+"F0.wireOp",EDGE,"E25.1"),sQuery(id+"F0.wireOp",EDGE,"E25.2"),sQuery(id+"F0.wireOp",EDGE,"E25.3"),sQuery(id+"F0.wireOp",EDGE,"E25.4"),sQuery(id+"F0.wireOp",EDGE,"E25.5"),sQuery(id+"F0.wireOp",EDGE,"E25.6"),sQuery(id+"F0.wireOp",EDGE,"E25.7")])],"isStart":false});
            extrude(context, id + "F17", {"entities" : qUnion([Q0]), "endBound" : BoundingType.UP_TO_SURFACE, "depth" : 25 * mm, "endBoundEntityFace" : qUnion([Q1]), "offsetDistance" : 25 * mm});
        }
    });
